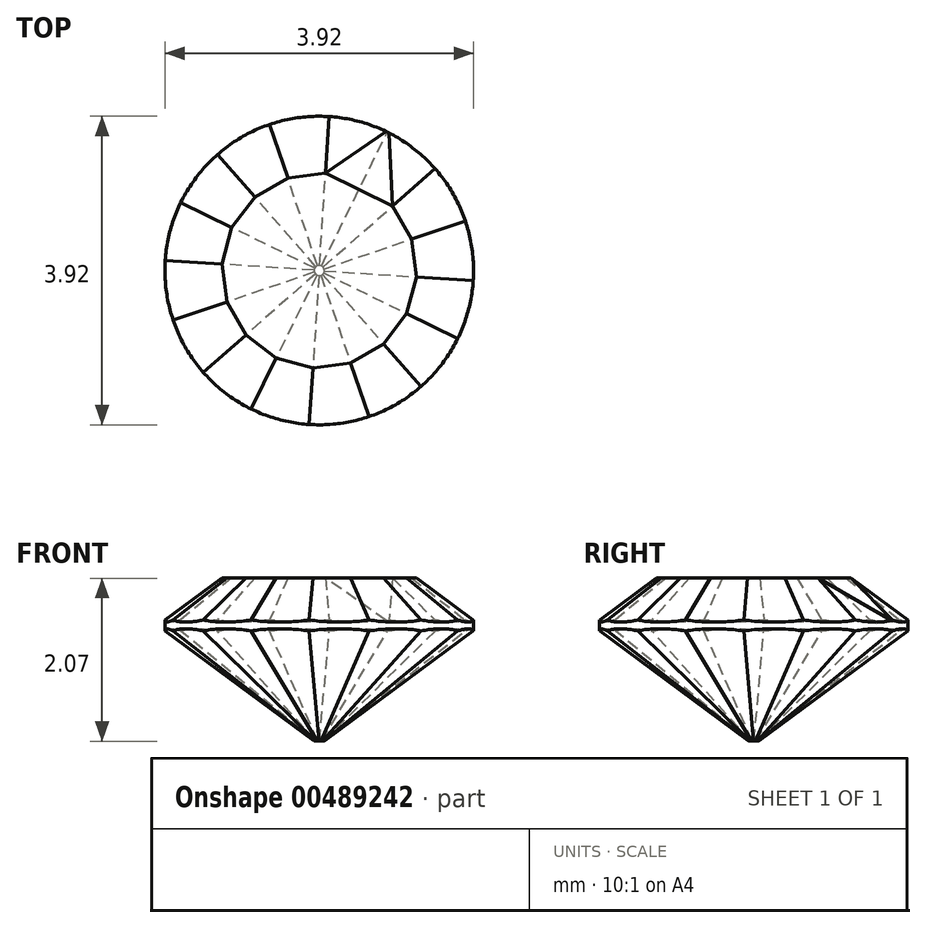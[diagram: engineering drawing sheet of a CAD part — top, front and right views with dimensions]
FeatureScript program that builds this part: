
annotation { "Feature Type Name" : "Feature", "Feature Type Description" : "" }
export const myFeature = defineFeature(function(context is Context, id is Id, definition is map)
    precondition{}
    {
        {
            var Q0;
            Q0=qCreatedBy(makeId("Top.planeOp"),FACE);
            var sketch = newSketch(context, id + "F0", { "sketchPlane" : qUnion([Q0])});
            skCircle(sketch, "E0.cCircle", {"center": v(0, 0) * mm, "radius": 1.96 * mm, "construction": true});
            skLineSegment(sketch, "E0.0", {"start": v(1.5, 1.32) * mm, "end": v(1.9, 0.64) * mm});
            skLineSegment(sketch, "E0.1", {"start": v(1.9, 0.64) * mm, "end": v(2, -0.13) * mm});
            skLineSegment(sketch, "E0.2", {"start": v(2, -0.13) * mm, "end": v(1.8, -0.88) * mm});
            skLineSegment(sketch, "E0.3", {"start": v(1.8, -0.88) * mm, "end": v(1.32, -1.5) * mm});
            skLineSegment(sketch, "E0.4", {"start": v(1.32, -1.5) * mm, "end": v(0.64, -1.9) * mm});
            skLineSegment(sketch, "E0.5", {"start": v(0.64, -1.9) * mm, "end": v(-0.13, -2) * mm});
            skLineSegment(sketch, "E0.6", {"start": v(-0.13, -2) * mm, "end": v(-0.88, -1.8) * mm});
            skLineSegment(sketch, "E0.7", {"start": v(-0.88, -1.8) * mm, "end": v(-1.5, -1.32) * mm});
            skLineSegment(sketch, "E0.8", {"start": v(-1.5, -1.32) * mm, "end": v(-1.9, -0.64) * mm});
            skLineSegment(sketch, "E0.9", {"start": v(-1.9, -0.64) * mm, "end": v(-2, 0.13) * mm});
            skLineSegment(sketch, "E0.10", {"start": v(-2, 0.13) * mm, "end": v(-1.8, 0.88) * mm});
            skLineSegment(sketch, "E0.11", {"start": v(-1.8, 0.88) * mm, "end": v(-1.32, 1.5) * mm});
            skLineSegment(sketch, "E0.12", {"start": v(-1.32, 1.5) * mm, "end": v(-0.64, 1.9) * mm});
            skLineSegment(sketch, "E0.13", {"start": v(-0.64, 1.9) * mm, "end": v(0.13, 2) * mm});
            skLineSegment(sketch, "E0.14", {"start": v(0.13, 2) * mm, "end": v(0.88, 1.8) * mm});
            skLineSegment(sketch, "E0.15", {"start": v(0.88, 1.8) * mm, "end": v(1.5, 1.32) * mm});
            skPoint(sketch, "E0.0.midPoint", {"position": v(1.7, 0.98) * mm});
            skSolve(sketch);
        }
        {
            var Q0;
            Q0 = qSketchRegion(id + "F0", true);
            extrude(context, id + "F1", {"entities" : qUnion([Q0]), "oppositeDirection" : true, "depth" : (2.36 * 0.6) * mm, "hasDraft" : true, "draftAngle" : 53 * degree, "draftPullDirection" : true});
        }
        {
            var Q0;
            Q0=makeQuery(id+"F1.opExtrude","CAP_FACE",FACE,{"disambiguationData":[OSD([sQuery(id+"F0.wireOp",EDGE,"E0.0"),sQuery(id+"F0.wireOp",EDGE,"E0.1"),sQuery(id+"F0.wireOp",EDGE,"E0.2"),sQuery(id+"F0.wireOp",EDGE,"E0.3"),sQuery(id+"F0.wireOp",EDGE,"E0.4"),sQuery(id+"F0.wireOp",EDGE,"E0.5"),sQuery(id+"F0.wireOp",EDGE,"E0.6"),sQuery(id+"F0.wireOp",EDGE,"E0.7"),sQuery(id+"F0.wireOp",EDGE,"E0.8"),sQuery(id+"F0.wireOp",EDGE,"E0.9"),sQuery(id+"F0.wireOp",EDGE,"E0.10"),sQuery(id+"F0.wireOp",EDGE,"E0.11"),sQuery(id+"F0.wireOp",EDGE,"E0.12"),sQuery(id+"F0.wireOp",EDGE,"E0.13"),sQuery(id+"F0.wireOp",EDGE,"E0.14"),sQuery(id+"F0.wireOp",EDGE,"E0.15")])],"isStart":true});
            extrude(context, id + "F2", {"entities" : qUnion([Q0]), "operationType" : NewBodyOperationType.ADD, "depth" : (2.36 * 0.04) * mm});
        }
        {
            var Q0;
            Q0=makeQuery(id+"F2.opExtrude","CAP_FACE",FACE,{"disambiguationData":[OSD([sQuery(id+"F0.wireOp",EDGE,"E0.0"),sQuery(id+"F0.wireOp",EDGE,"E0.1"),sQuery(id+"F0.wireOp",EDGE,"E0.2"),sQuery(id+"F0.wireOp",EDGE,"E0.3"),sQuery(id+"F0.wireOp",EDGE,"E0.4"),sQuery(id+"F0.wireOp",EDGE,"E0.5"),sQuery(id+"F0.wireOp",EDGE,"E0.6"),sQuery(id+"F0.wireOp",EDGE,"E0.7"),sQuery(id+"F0.wireOp",EDGE,"E0.8"),sQuery(id+"F0.wireOp",EDGE,"E0.9"),sQuery(id+"F0.wireOp",EDGE,"E0.10"),sQuery(id+"F0.wireOp",EDGE,"E0.11"),sQuery(id+"F0.wireOp",EDGE,"E0.12"),sQuery(id+"F0.wireOp",EDGE,"E0.13"),sQuery(id+"F0.wireOp",EDGE,"E0.14"),sQuery(id+"F0.wireOp",EDGE,"E0.15")])],"isStart":false});
            extrude(context, id + "F3", {"entities" : qUnion([Q0]), "operationType" : NewBodyOperationType.ADD, "depth" : 0.56 * mm, "hasDraft" : true, "draftAngle" : 53 * degree, "draftPullDirection" : true});
        }
        {
            var Q0;
            Q0=makeQuery(id+"F3.opExtrude","SWEPT_FACE",FACE,{"disambiguationData":[OSD([sQuery(id+"F0.wireOp",EDGE,"E0.15")])]});
            var sketch = newSketch(context, id + "F4", { "sketchPlane" : qUnion([Q0])});
            skLineSegment(sketch, "E1", {"start": v(0.51, 0.37) * mm, "end": v(0.46, 1.5) * mm, "construction": true});
            skSolve(sketch);
        }
        {
            var Q0;
            Q0=makeQuery(id+"F3.opExtrude","SWEPT_FACE",FACE,{"disambiguationData":[OSD([sQuery(id+"F0.wireOp",EDGE,"E0.14")])]});
            var sketch = newSketch(context, id + "F5", { "sketchPlane" : qUnion([Q0])});
            skLineSegment(sketch, "E2", {"start": v(0.7, 1.4) * mm, "end": v(-0.11, 0.62) * mm, "construction": true});
            skSolve(sketch);
        }
        {
            var Q0;
            Q0=makeQuery(id+"F3.opExtrude","CAP_FACE",FACE,{"disambiguationData":[OSD([sQuery(id+"F0.wireOp",EDGE,"E0.0"),sQuery(id+"F0.wireOp",EDGE,"E0.1"),sQuery(id+"F0.wireOp",EDGE,"E0.2"),sQuery(id+"F0.wireOp",EDGE,"E0.3"),sQuery(id+"F0.wireOp",EDGE,"E0.4"),sQuery(id+"F0.wireOp",EDGE,"E0.5"),sQuery(id+"F0.wireOp",EDGE,"E0.6"),sQuery(id+"F0.wireOp",EDGE,"E0.7"),sQuery(id+"F0.wireOp",EDGE,"E0.8"),sQuery(id+"F0.wireOp",EDGE,"E0.9"),sQuery(id+"F0.wireOp",EDGE,"E0.10"),sQuery(id+"F0.wireOp",EDGE,"E0.11"),sQuery(id+"F0.wireOp",EDGE,"E0.12"),sQuery(id+"F0.wireOp",EDGE,"E0.13"),sQuery(id+"F0.wireOp",EDGE,"E0.14"),sQuery(id+"F0.wireOp",EDGE,"E0.15")])],"isStart":false});
            var sketch = newSketch(context, id + "F6", { "sketchPlane" : qUnion([Q0])});
            skLineSegment(sketch, "E3", {"start": v(0.93, 0.82) * mm, "end": v(0.08, 1.24) * mm, "construction": true});
            skSolve(sketch);
        }
        {
            var Q0;
            Q0=sQuery(id+"F4.wireOp",EDGE,"E1");
            cPoint(context, id + "F7", {"entities" : qUnion([Q0]), "parameter" : 0.5});
        }
        {
            var Q0;
            Q0=sQuery(id+"F5.wireOp",EDGE,"E2");
            cPoint(context, id + "F8", {"entities" : qUnion([Q0]), "parameter" : 0.5});
        }
        {
            var Q0;
            Q0=sQuery(id+"F6.wireOp",EDGE,"E3");
            cPoint(context, id + "F9", {"entities" : qUnion([Q0]), "parameter" : 0.5});
        }
        {
            var Q0;
            Q0 = qCreatedBy(id + "F7" ,VERTEX);
            var Q1;
            Q1 = qCreatedBy(id + "F8" ,VERTEX);
            var Q2;
            Q2 = qCreatedBy(id + "F9" ,VERTEX);
            cPlane(context, id + "F10", {"entities" : qUnion([Q0, Q1, Q2]), "cplaneType" : CPlaneType.THREE_POINT, "offset" : 25 * mm, "width" : 150 * mm, "height" : 150 * mm});
        }
        {
            var Q0;
            Q0=qCreatedBy(id+"F10.planeOp",FACE);
            var sketch = newSketch(context, id + "F11", { "sketchPlane" : qUnion([Q0])});
            skLineSegment(sketch, "E4.0", {"start": v(0.67, -0.38) * mm, "end": v(0.62, -1.5) * mm});
            skLineSegment(sketch, "E4.1", {"start": v(0.62, -1.5) * mm, "end": v(-0.2, -0.74) * mm});
            skLineSegment(sketch, "E4.2", {"start": v(0.67, -0.38) * mm, "end": v(-0.2, -0.74) * mm});
            skSolve(sketch);
        }
        {
            var Q0;
            Q0 = qSketchRegion(id + "F11", true);
            extrude(context, id + "F12", {"entities" : qUnion([Q0]), "operationType" : NewBodyOperationType.REMOVE, "oppositeDirection" : true, "depth" : 25 * mm});
        }
        {
            var Q0;
            Q0=qCreatedBy(makeId("Front.planeOp"),FACE);
            var sketch = newSketch(context, id + "F13", { "sketchPlane" : qUnion([Q0])});
            skLineSegment(sketch, "E5", {"start": v(0, -1.8) * mm, "end": v(0, 1.8) * mm, "construction": true});
            skSolve(sketch);
        }
        {
            var Q0;
            Q0=makeQuery(id+"F3.opExtrude","CAP_FACE",FACE,{"disambiguationData":[OSD([sQuery(id+"F0.wireOp",EDGE,"E0.0"),sQuery(id+"F0.wireOp",EDGE,"E0.1"),sQuery(id+"F0.wireOp",EDGE,"E0.2"),sQuery(id+"F0.wireOp",EDGE,"E0.3"),sQuery(id+"F0.wireOp",EDGE,"E0.4"),sQuery(id+"F0.wireOp",EDGE,"E0.5"),sQuery(id+"F0.wireOp",EDGE,"E0.6"),sQuery(id+"F0.wireOp",EDGE,"E0.7"),sQuery(id+"F0.wireOp",EDGE,"E0.8"),sQuery(id+"F0.wireOp",EDGE,"E0.9"),sQuery(id+"F0.wireOp",EDGE,"E0.10"),sQuery(id+"F0.wireOp",EDGE,"E0.11"),sQuery(id+"F0.wireOp",EDGE,"E0.12"),sQuery(id+"F0.wireOp",EDGE,"E0.13"),sQuery(id+"F0.wireOp",EDGE,"E0.14"),sQuery(id+"F0.wireOp",EDGE,"E0.15")])],"isStart":false});
            var sketch = newSketch(context, id + "F14", { "sketchPlane" : qUnion([Q0])});
            skCircle(sketch, "E6", {"center": v(0, 0) * mm, "radius": 1.96 * mm});
            skSolve(sketch);
        }
        {
            var Q0;
            Q0 = qSketchRegion(id + "F14", true);
            extrude(context, id + "F15", {"entities" : qUnion([Q0]), "operationType" : NewBodyOperationType.INTERSECT, "oppositeDirection" : true, "depth" : 25 * mm});
        }
    });
